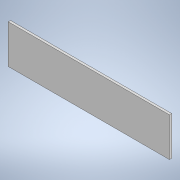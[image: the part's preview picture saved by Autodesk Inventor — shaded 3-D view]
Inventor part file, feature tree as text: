
AUTODESK INVENTOR PART (.ipt)
format: ipt  version: 2021 (Build 250183000, 183)  size: 91,136 bytes
history: native  units: in
note: dims shown in document units (in); Inventor stores cm internally (conversion verified against a paired STEP export)
features: extrude x1, sketch x1
ambient origin geometry x8: Origin, YZ Plane, XZ Plane, XY Plane, X Axis, Y Axis, Z Axis, Center Point
bodies: Solid1 (feature_tree)
feature tree (2):
  extrude  "Extrusion1"  Depth=1.683in
  sketch  "Sketch1"  dims[d0=7.0in d1=1.683in d2=0.1in d3=0.0in]
